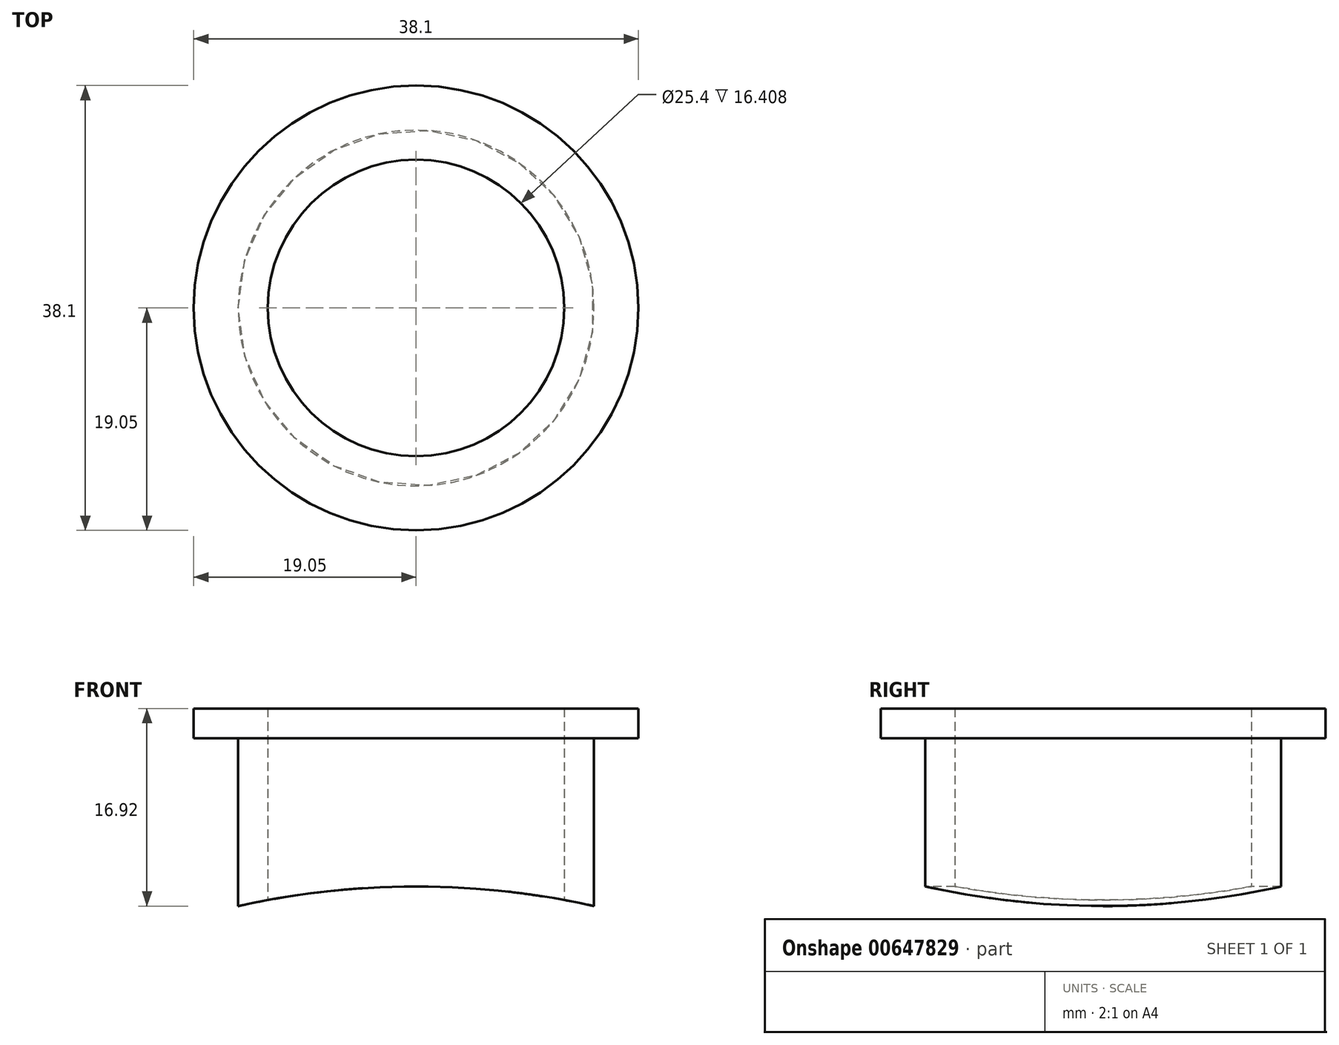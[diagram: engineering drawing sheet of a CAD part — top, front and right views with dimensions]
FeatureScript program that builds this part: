
annotation { "Feature Type Name" : "Feature", "Feature Type Description" : "" }
export const myFeature = defineFeature(function(context is Context, id is Id, definition is map)
    precondition{}
    {
        {
            var Q0;
            Q0=qCreatedBy(makeId("Front.planeOp"),FACE);
            var sketch = newSketch(context, id + "F0", { "sketchPlane" : qUnion([Q0])});
            skLineSegment(sketch, "E0", {"start": v(0, 0) * mm, "end": v(-12.7, 0) * mm, "construction": true});
            skLineSegment(sketch, "E1", {"start": v(-12.7, 0) * mm, "end": v(-15.24, 0) * mm});
            skLineSegment(sketch, "E2", {"start": v(-15.24, 0) * mm, "end": v(-15.24, 12.7) * mm});
            skLineSegment(sketch, "E3", {"start": v(-15.24, 12.7) * mm, "end": v(-12.7, 12.7) * mm});
            skLineSegment(sketch, "E4", {"start": v(-12.7, 12.7) * mm, "end": v(-12.7, 0) * mm});
            skLineSegment(sketch, "E5", {"start": v(-12.7, 12.7) * mm, "end": v(-12.7, 15.24) * mm});
            skLineSegment(sketch, "E6", {"start": v(-12.7, 15.24) * mm, "end": v(-19.05, 15.24) * mm});
            skLineSegment(sketch, "E7", {"start": v(-19.05, 15.24) * mm, "end": v(-19.05, 12.7) * mm});
            skLineSegment(sketch, "E8", {"start": v(-19.05, 12.7) * mm, "end": v(-15.24, 12.7) * mm});
            skLineSegment(sketch, "E9", {"start": v(0, 0) * mm, "end": v(0, 20.35) * mm, "construction": true});
            skSolve(sketch);
        }
        {
            var Q0;
            Q0 = qSketchRegion(id + "F0", true);
            var Q1;
            Q1=sQuery(id+"F0.wireOp",EDGE,"E9");
            revolve(context, id + "F1", {"entities" : qUnion([Q0]), "axis" : qUnion([Q1]), "revolveType" : RevolveType.FULL});
        }
        {
            var Q0;
            Q0=qCreatedBy(makeId("Front.planeOp"),FACE);
            var sketch = newSketch(context, id + "F2", { "sketchPlane" : qUnion([Q0])});
            skLineSegment(sketch, "E10", {"start": v(0, 0) * mm, "end": v(0, -69.85) * mm, "construction": true});
            skCircle(sketch, "E11", {"center": v(0, -69.85) * mm, "radius": 69.85 * mm});
            skSolve(sketch);
        }
        {
            var Q0;
            Q0=makeQuery(id+"F1.opRevolve","SWEPT_FACE",FACE,{"disambiguationData":[OSD([sQuery(id+"F0.wireOp",EDGE,"E1")])]});
            extrude(context, id + "F3", {"entities" : qUnion([Q0]), "operationType" : NewBodyOperationType.ADD, "depth" : 25.4 * mm, "offsetDistance" : 25.4 * mm});
        }
        {
            var Q0;
            Q0=makeQuery(id+"F2.imprint","IMPRINT",FACE,{"disambiguationData":[TD([[makeQuery(id+"F2.imprint","IMPRINT",EDGE,{"derivedFrom":sQuery(id+"F2.wireOp",EDGE,"E11")}),1.0]])]});
            extrude(context, id + "F4", {"entities" : qUnion([Q0]), "operationType" : NewBodyOperationType.REMOVE, "oppositeDirection" : true, "depth" : 25.4 * mm, "offsetDistance" : 25.4 * mm, "hasSecondDirection" : true, "secondDirectionOppositeDirection" : false, "secondDirectionDepth" : 25.4 * mm});
        }
    });
